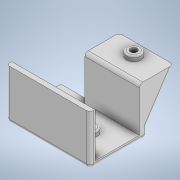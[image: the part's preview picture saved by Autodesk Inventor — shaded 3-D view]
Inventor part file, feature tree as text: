
AUTODESK INVENTOR PART (.ipt)
format: ipt  version: 2020 (Build 240168000, 168)  size: 270,848 bytes
history: native  units: in
note: dims shown in document units (in); Inventor stores cm internally (conversion verified against a paired STEP export)
features: extrude x14, sketch x14, fillet x3
ambient origin geometry x8: Origin, YZ Plane, XZ Plane, XY Plane, X Axis, Y Axis, Z Axis, Center Point
bodies: Solid1 (feature_tree)
feature tree (31):
  extrude  "Extrusion1"  Depth=1.2756in
  extrude  "Extrusion4"  Depth=0.1181in
  extrude  "Extrusion5"  Depth=0.1181in
  extrude  "Extrusion6"  Depth=0.1181in
  extrude  "Extrusion7"  Depth=0.1181in TaperAngle=0.0deg
  extrude  "Extrusion8"  Depth=0.1575in
  extrude  "Extrusion15"  Depth=0.2362in
  extrude  "Extrusion23"  Depth=0.1181in TaperAngle=0.0deg
  extrude  "Extrusion24"  Depth=1.2756in
  extrude  "Extrusion25"  Depth=1.0394in TaperAngle=0.0deg
  extrude  "Extrusion26"  Depth=0.1181in
  extrude  "Extrusion27"  Depth=0.6811in TaperAngle=0.0deg
  extrude  "Extrusion28"  Depth=1.2756in
  fillet  "Fillet3"  Radius=1.2756in
  fillet  "Fillet4"  Radius=0.3346in
  extrude  "Extrusion29"  Depth=0.1181in
  fillet  "Fillet5"  Radius=1.0394in
  sketch  "Sketch1"  dims[d0=1.6142in d1=1.2756in]
  sketch  "Sketch4"  dims[d2=0.1181in d3=0.0in d12=0.8465in]
  sketch  "Sketch5"  dims[d13=0.1181in d14=0.0in d15=0.8465in]
  sketch  "Sketch6"  dims[d16=0.1181in d17=0.0in d20=0.3346in]
  sketch  "Sketch7"  dims[d21=0.3346in d22=0.1181in d23=0.0in]
  sketch  "Sketch8"  dims[d24=0.1575in d25=0.1575in]
  sketch  "Sketch15"  dims[d26=0.2362in d27=0.0in d28=0.2362in]
  sketch  "Sketch23"  dims[d29=0.2362in d30=0.1181in d31=0.0in]
  sketch  "Sketch24"  dims[d54=0.3425in d55=0.0in d81=1.2756in]
  sketch  "Sketch25"  dims[d82=0.1181in d83=1.0394in d84=0.0in]
  sketch  "Sketch26"  dims[d85=0.1181in d86=0.1181in]
  sketch  "Sketch27"  dims[d87=0.1181in d88=0.6811in d89=0.0in]
  sketch  "Sketch28"  dims[d90=1.2756in d91=0.0in d92=0.1575in d93=1.2756in d94=0.0in d95=0.3346in]
  sketch  "Sketch29"  dims[d96=0.1181in d97=0.0in d98=0.1181in d99=1.0394in d100=0.0in d101=0.0394in d102=0.0787in d103=0.2362in d104=0.1181in d105=0.0in d106=0.0787in d10=0.0197in d11=0.0344in d65=0.0197in d66=0.0344in d67=0.0197in d68=0.0344in]
